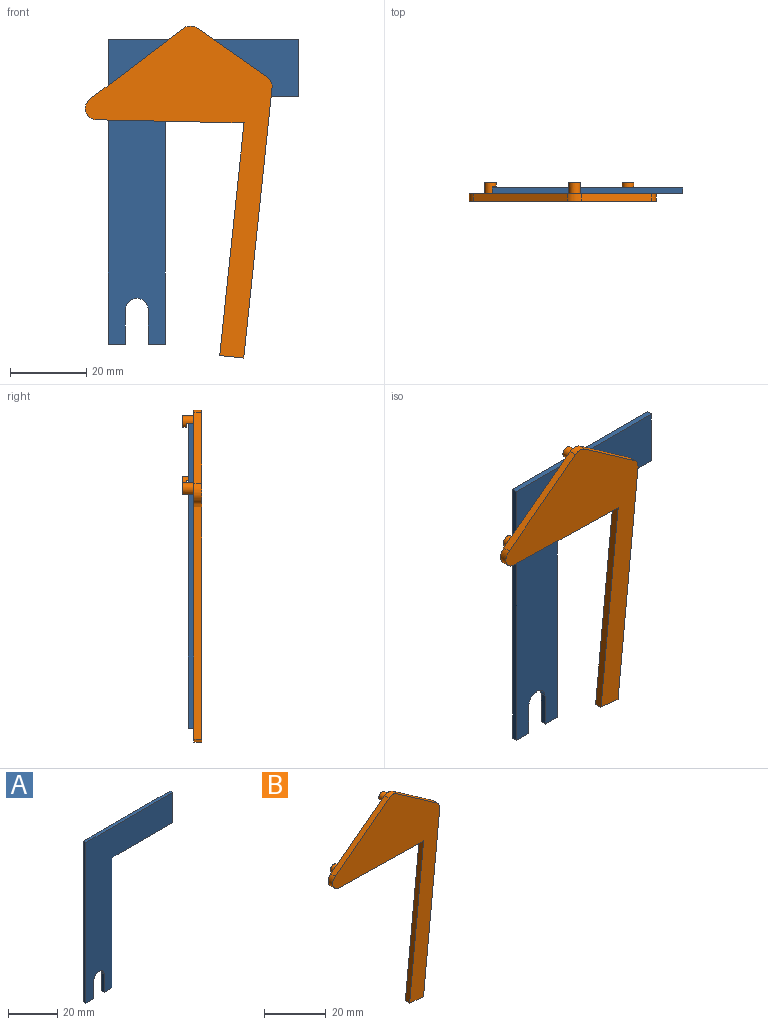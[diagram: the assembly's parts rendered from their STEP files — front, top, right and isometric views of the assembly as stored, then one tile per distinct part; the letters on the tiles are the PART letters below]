
ASSEMBLY  parts=2 mates=3
PART A: 12 faces, bbox 50x1.5x80 mm
  f0: plane 4.5x1.5mm, normal (0,0,-1), area 6.7mm2, adj f2,f7,f8,f10
  f1: plane 50x1.5mm, normal (0,0,1), area 75mm2, adj f2,f6,f7,f8
  f2: plane 80x1.5mm, normal (-1,0,0), area 120mm2, adj f0,f1,f7,f8
  f3: plane 4.5x1.5mm, normal (0,0,-1), area 6.8mm2, adj f4,f7,f8,f11
  f4: plane 65x1.5mm, normal (1,0,0), area 97.5mm2, adj f3,f5,f7,f8
  f5: plane 35x1.5mm, normal (0,0,-1), area 52.5mm2, adj f4,f6,f7,f8
  f6: plane 15x1.5mm, normal (1,0,0), area 22.5mm2, adj f1,f5,f7,f8
  f7: plane 80x50mm, normal (0,-1,0), area 1656.9mm2, adj f0,f1,f2,f3,f4,f5,f6,f9
  f8: plane 80x50mm, normal (0,1,0), area 1656.9mm2, adj f0,f1,f2,f3,f4,f5,f6,f9
  f9: cylinder r=3mm len=6mm, axis (0,-1,0), area 14.1mm2, adj f7,f8,f10,f11
  f10: plane 9x1.5mm, normal (1,0,0), area 13.5mm2, adj f0,f7,f8,f9
  f11: plane 9x1.5mm, normal (-1,0,0), area 13.5mm2, adj f3,f7,f8,f9
PART B: 23 faces, bbox 49.1x5x87.2 mm
  f0: plane 24.65x18.63mm, normal (-0.6,0,0.8), area 61.8mm2, adj f6,f7,f14,f16
  f1: plane 38.75x2mm, normal (-0.02,0,-1), area 77.5mm2, adj f2,f6,f7,f14
  f2: plane 61.07x6.39mm, normal (-0.99,0,0.1), area 122.8mm2, adj f1,f3,f6,f7
  f3: plane 6.32x2mm, normal (-0.1,0,-0.99), area 12.7mm2, adj f2,f4,f6,f7
  f4: plane 70.95x7.43mm, normal (0.99,0,-0.1), area 142.7mm2, adj f3,f6,f7,f15
  f5: plane 18.41x12.92mm, normal (0.57,0,0.82), area 45mm2, adj f6,f7,f15,f16
  f6: plane 87.19x49.06mm, normal (0,-1,0), area 1200.3mm2, adj f0,f1,f2,f3,f4,f5,f14,f15
  f7: plane 87.19x49.06mm, normal (0,1,0), area 1188.2mm2, adj f0,f1,f2,f3,f4,f5,f8,f10
  f8: cylinder r=1.5mm len=3mm, axis (0,-1,0), area 20.9mm2, adj f7,f9,f21,f22
  f9: plane 3x3mm, normal (0,1,0), area 7.1mm2, adj f8
  f10: cylinder r=1.5mm len=3mm, axis (0,-1,0), area 20.9mm2, adj f7,f11,f19,f20
  f11: plane 3x3mm, normal (0,1,0), area 7.1mm2, adj f10
  f12: cylinder r=1.5mm len=3mm, axis (0,-1,0), area 16.8mm2, adj f7,f13,f17,f18
  f13: plane 3x3mm, normal (0,1,0), area 7.1mm2, adj f12
  f14: cylinder r=3mm len=5.39mm, axis (0,1,0), area 14.8mm2, adj f0,f1,f6,f7
  f15: cylinder r=3mm len=2.77mm, axis (0,1,0), area 6.4mm2, adj f4,f5,f6,f7
  f16: cylinder r=3mm len=3.53mm, axis (0,1,0), area 7.6mm2, adj f0,f5,f6,f7
  f17: plane 2.83x2mm, normal (0,0,-1), area 5.7mm2, adj f7,f12,f18
  f18: plane 3x2mm, normal (0,-1,0), area 5mm2, adj f12,f17
  f19: plane 2.83x2mm, normal (1,0,0), area 5.7mm2, adj f7,f10,f20
  f20: plane 2.83x1mm, normal (0,-1,0), area 2.1mm2, adj f10,f19
  f21: plane 2.83x2mm, normal (0,0,-1), area 5.7mm2, adj f7,f8,f22
  f22: plane 2.83x1mm, normal (0,-1,0), area 2.1mm2, adj f8,f21
PLACE A t=(4.91,-0.34,0.52)mm
PLACE B t=(4.91,-1.09,0.52)mm
MATE planar B.f19 <-> A.f2  axis (1,0,0) through (4.91,-0.09,-16.56)mm
MATE planar A.f1 <-> B.f21  axis (0,0,1) through (29.91,-0.34,0.52)mm
MATE planar A.f7 <-> B.f7  axis (0,-1,0) through (20.34,-1.09,-27.77)mm
